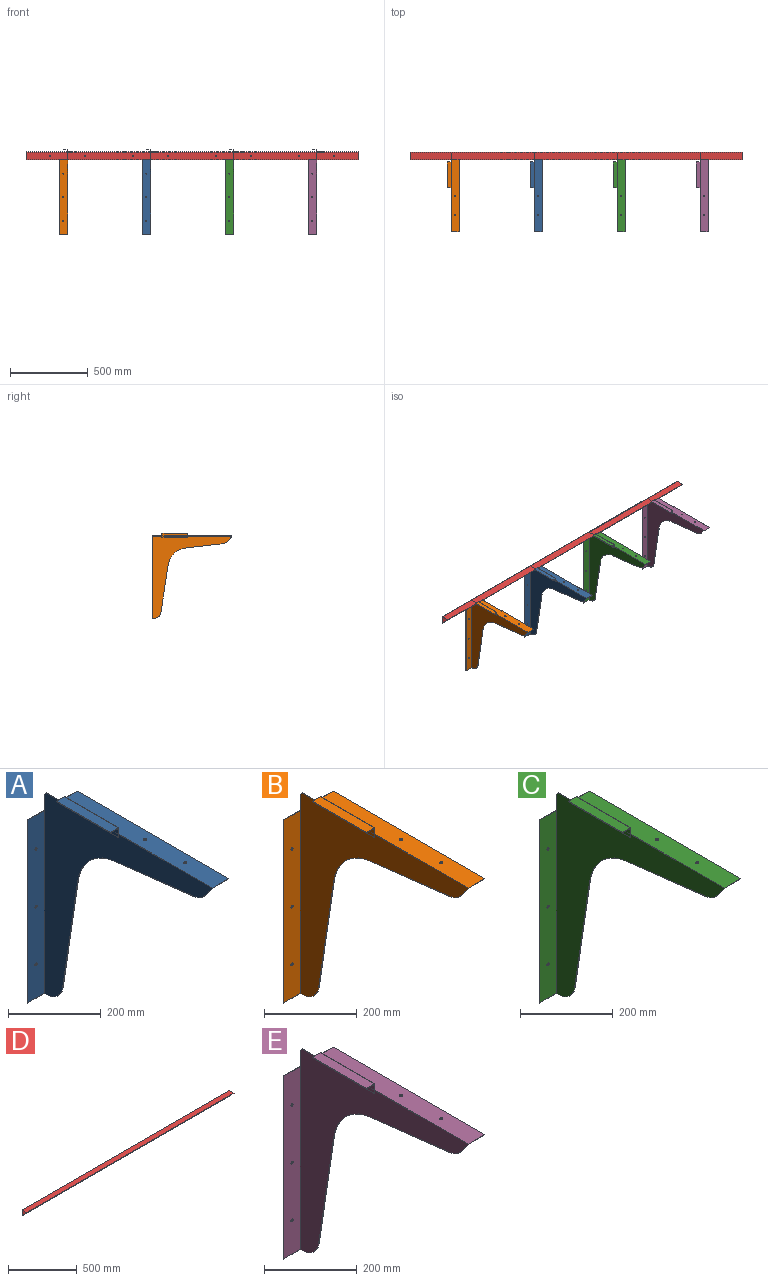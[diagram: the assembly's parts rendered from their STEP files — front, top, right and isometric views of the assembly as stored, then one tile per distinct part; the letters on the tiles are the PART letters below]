
ASSEMBLY  parts=5 mates=4
PART A: 33 faces, bbox 101.6x513.2x550.9 mm
  f0: plane 165.1x23.81mm, normal (-1,0,0), area 3931.4mm2, adj f2,f3,f4,f6
  f1: plane 165.1x25.4mm, normal (0,0,1), area 4193.5mm2, adj f2,f4,f5,f7
  f2: plane 25.4x25.4mm, normal (0,1,0), area 78.1mm2, adj f0,f1,f3,f5,f6,f7,f19
  f3: plane 165.1x1.59mm, normal (0,0,-1), area 262.1mm2, adj f0,f2,f4,f19
  f4: plane 25.4x25.4mm, normal (0,-1,0), area 78.1mm2, adj f0,f1,f3,f5,f6,f7,f19
  f5: plane 165.1x17.46mm, normal (1,0,0), area 2883.1mm2, adj f1,f2,f4,f22
  f6: plane 165.1x23.81mm, normal (0,0,-1), area 3931.4mm2, adj f0,f2,f4,f7
  f7: plane 165.1x1.59mm, normal (-1,0,0), area 262.1mm2, adj f1,f2,f4,f6
  f8: plane 42.86x1.59mm, normal (0,0,1), area 68mm2, adj f9,f18,f19,f21
  f9: plane 6.35x6.35mm, normal (0,0.71,0.71), area 14.3mm2, adj f8,f17,f18,f19
  f10: plane 50.8x30mm, normal (0,-0.81,-0.59), area 155.8mm2, adj f11,f18,f19,f20,f22,f23
  f11: cylinder r=50.8mm len=35.21mm, axis (-1,0,0), area 66.5mm2, adj f10,f12,f18,f19
  f12: plane 241.42x27.7mm, normal (0,-0.11,-0.99), area 385.8mm2, adj f11,f13,f18,f19
  f13: cylinder r=127mm len=111.09mm, axis (-1,0,0), area 263.3mm2, adj f12,f14,f18,f19
  f14: plane 304.89x46.19mm, normal (0,-0.99,-0.15), area 489.5mm2, adj f13,f15,f18,f19
  f15: cylinder r=50.8mm len=50.23mm, axis (-1,0,0), area 114.6mm2, adj f14,f16,f18,f19
  f16: plane 52.39x7.12mm, normal (0,0,-1), area 91.9mm2, adj f15,f18,f19,f24,f25,f27
  f17: plane 42.86x1.59mm, normal (0,1,0), area 68mm2, adj f9,f18,f19,f26
  f18: plane 531.81x512.03mm, normal (1,0,0), area 74022.7mm2, adj f8,f9,f10,f11,f12,f13,f14,f15
  f19: plane 533.4x511.61mm, normal (-1,0,0), area 72679.2mm2, adj f2,f3,f4,f8,f9,f10,f11,f12
  f20: plane 461.23x49.21mm, normal (0,0,-1), area 22626.8mm2, adj f10,f18,f21,f23,f31,f32
  f21: plane 50.8x1.59mm, normal (0,1,0), area 80.6mm2, adj f8,f19,f20,f22,f23
  f22: plane 462.4x50.8mm, normal (0,0,1), area 23418mm2, adj f5,f10,f19,f21,f23,f31,f32
  f23: plane 462.4x1.59mm, normal (1,0,0), area 733.1mm2, adj f10,f20,f21,f22
  f24: plane 482.6x50.8mm, normal (0,-1,0), area 24421.1mm2, adj f16,f19,f26,f27,f28,f29,f30
  f25: plane 482.6x52.39mm, normal (0,1,0), area 25187.2mm2, adj f16,f18,f26,f27,f28,f29,f30
  f26: plane 52.39x1.59mm, normal (0,0,1), area 83.2mm2, adj f17,f18,f24,f25,f27
  f27: plane 482.6x1.59mm, normal (-1,0,0), area 766.1mm2, adj f16,f24,f25,f26
  f28: cylinder r=3.17mm len=6.35mm, axis (0,-1,0), area 31.7mm2, adj f24,f25
  f29: cylinder r=3.17mm len=6.35mm, axis (0,-1,0), area 31.7mm2, adj f24,f25
  f30: cylinder r=3.17mm len=6.35mm, axis (0,-1,0), area 31.7mm2, adj f24,f25
  f31: cylinder r=3.38mm len=6.76mm, axis (0,0,-1), area 33.7mm2, adj f20,f22
  f32: cylinder r=3.38mm len=6.76mm, axis (0,0,-1), area 33.7mm2, adj f20,f22
PART B: 33 faces, bbox 101.6x513.2x550.9 mm
  f0: plane 165.1x23.81mm, normal (-1,0,0), area 3931.4mm2, adj f2,f3,f4,f6
  f1: plane 165.1x25.4mm, normal (0,0,1), area 4193.5mm2, adj f2,f4,f5,f7
  f2: plane 25.4x25.4mm, normal (0,1,0), area 78.1mm2, adj f0,f1,f3,f5,f6,f7,f19
  f3: plane 165.1x1.59mm, normal (0,0,-1), area 262.1mm2, adj f0,f2,f4,f19
  f4: plane 25.4x25.4mm, normal (0,-1,0), area 78.1mm2, adj f0,f1,f3,f5,f6,f7,f19
  f5: plane 165.1x17.46mm, normal (1,0,0), area 2883.1mm2, adj f1,f2,f4,f22
  f6: plane 165.1x23.81mm, normal (0,0,-1), area 3931.4mm2, adj f0,f2,f4,f7
  f7: plane 165.1x1.59mm, normal (-1,0,0), area 262.1mm2, adj f1,f2,f4,f6
  f8: plane 42.86x1.59mm, normal (0,0,1), area 68mm2, adj f9,f18,f19,f21
  f9: plane 6.35x6.35mm, normal (0,0.71,0.71), area 14.3mm2, adj f8,f17,f18,f19
  f10: plane 50.8x30mm, normal (0,-0.81,-0.59), area 155.8mm2, adj f11,f18,f19,f20,f22,f23
  f11: cylinder r=50.8mm len=35.21mm, axis (-1,0,0), area 66.5mm2, adj f10,f12,f18,f19
  f12: plane 241.42x27.7mm, normal (0,-0.11,-0.99), area 385.8mm2, adj f11,f13,f18,f19
  f13: cylinder r=127mm len=111.09mm, axis (-1,0,0), area 263.3mm2, adj f12,f14,f18,f19
  f14: plane 304.89x46.19mm, normal (0,-0.99,-0.15), area 489.5mm2, adj f13,f15,f18,f19
  f15: cylinder r=50.8mm len=50.23mm, axis (-1,0,0), area 114.6mm2, adj f14,f16,f18,f19
  f16: plane 52.39x7.12mm, normal (0,0,-1), area 91.9mm2, adj f15,f18,f19,f24,f25,f27
  f17: plane 42.86x1.59mm, normal (0,1,0), area 68mm2, adj f9,f18,f19,f26
  f18: plane 531.81x512.03mm, normal (1,0,0), area 74022.7mm2, adj f8,f9,f10,f11,f12,f13,f14,f15
  f19: plane 533.4x511.61mm, normal (-1,0,0), area 72679.2mm2, adj f2,f3,f4,f8,f9,f10,f11,f12
  f20: plane 461.23x49.21mm, normal (0,0,-1), area 22626.8mm2, adj f10,f18,f21,f23,f31,f32
  f21: plane 50.8x1.59mm, normal (0,1,0), area 80.6mm2, adj f8,f19,f20,f22,f23
  f22: plane 462.4x50.8mm, normal (0,0,1), area 23418mm2, adj f5,f10,f19,f21,f23,f31,f32
  f23: plane 462.4x1.59mm, normal (1,0,0), area 733.1mm2, adj f10,f20,f21,f22
  f24: plane 482.6x50.8mm, normal (0,-1,0), area 24421.1mm2, adj f16,f19,f26,f27,f28,f29,f30
  f25: plane 482.6x52.39mm, normal (0,1,0), area 25187.2mm2, adj f16,f18,f26,f27,f28,f29,f30
  f26: plane 52.39x1.59mm, normal (0,0,1), area 83.2mm2, adj f17,f18,f24,f25,f27
  f27: plane 482.6x1.59mm, normal (-1,0,0), area 766.1mm2, adj f16,f24,f25,f26
  f28: cylinder r=3.17mm len=6.35mm, axis (0,-1,0), area 31.7mm2, adj f24,f25
  f29: cylinder r=3.17mm len=6.35mm, axis (0,-1,0), area 31.7mm2, adj f24,f25
  f30: cylinder r=3.17mm len=6.35mm, axis (0,-1,0), area 31.7mm2, adj f24,f25
  f31: cylinder r=3.38mm len=6.76mm, axis (0,0,-1), area 33.7mm2, adj f20,f22
  f32: cylinder r=3.38mm len=6.76mm, axis (0,0,-1), area 33.7mm2, adj f20,f22
PART C: 33 faces, bbox 101.6x513.2x550.9 mm
  f0: plane 165.1x23.81mm, normal (-1,0,0), area 3931.4mm2, adj f2,f3,f4,f6
  f1: plane 165.1x25.4mm, normal (0,0,1), area 4193.5mm2, adj f2,f4,f5,f7
  f2: plane 25.4x25.4mm, normal (0,1,0), area 78.1mm2, adj f0,f1,f3,f5,f6,f7,f19
  f3: plane 165.1x1.59mm, normal (0,0,-1), area 262.1mm2, adj f0,f2,f4,f19
  f4: plane 25.4x25.4mm, normal (0,-1,0), area 78.1mm2, adj f0,f1,f3,f5,f6,f7,f19
  f5: plane 165.1x17.46mm, normal (1,0,0), area 2883.1mm2, adj f1,f2,f4,f22
  f6: plane 165.1x23.81mm, normal (0,0,-1), area 3931.4mm2, adj f0,f2,f4,f7
  f7: plane 165.1x1.59mm, normal (-1,0,0), area 262.1mm2, adj f1,f2,f4,f6
  f8: plane 42.86x1.59mm, normal (0,0,1), area 68mm2, adj f9,f18,f19,f21
  f9: plane 6.35x6.35mm, normal (0,0.71,0.71), area 14.3mm2, adj f8,f17,f18,f19
  f10: plane 50.8x30mm, normal (0,-0.81,-0.59), area 155.8mm2, adj f11,f18,f19,f20,f22,f23
  f11: cylinder r=50.8mm len=35.21mm, axis (-1,0,0), area 66.5mm2, adj f10,f12,f18,f19
  f12: plane 241.42x27.7mm, normal (0,-0.11,-0.99), area 385.8mm2, adj f11,f13,f18,f19
  f13: cylinder r=127mm len=111.09mm, axis (-1,0,0), area 263.3mm2, adj f12,f14,f18,f19
  f14: plane 304.89x46.19mm, normal (0,-0.99,-0.15), area 489.5mm2, adj f13,f15,f18,f19
  f15: cylinder r=50.8mm len=50.23mm, axis (-1,0,0), area 114.6mm2, adj f14,f16,f18,f19
  f16: plane 52.39x7.12mm, normal (0,0,-1), area 91.9mm2, adj f15,f18,f19,f24,f25,f27
  f17: plane 42.86x1.59mm, normal (0,1,0), area 68mm2, adj f9,f18,f19,f26
  f18: plane 531.81x512.03mm, normal (1,0,0), area 74022.7mm2, adj f8,f9,f10,f11,f12,f13,f14,f15
  f19: plane 533.4x511.61mm, normal (-1,0,0), area 72679.2mm2, adj f2,f3,f4,f8,f9,f10,f11,f12
  f20: plane 461.23x49.21mm, normal (0,0,-1), area 22626.8mm2, adj f10,f18,f21,f23,f31,f32
  f21: plane 50.8x1.59mm, normal (0,1,0), area 80.6mm2, adj f8,f19,f20,f22,f23
  f22: plane 462.4x50.8mm, normal (0,0,1), area 23418mm2, adj f5,f10,f19,f21,f23,f31,f32
  f23: plane 462.4x1.59mm, normal (1,0,0), area 733.1mm2, adj f10,f20,f21,f22
  f24: plane 482.6x50.8mm, normal (0,-1,0), area 24421.1mm2, adj f16,f19,f26,f27,f28,f29,f30
  f25: plane 482.6x52.39mm, normal (0,1,0), area 25187.2mm2, adj f16,f18,f26,f27,f28,f29,f30
  f26: plane 52.39x1.59mm, normal (0,0,1), area 83.2mm2, adj f17,f18,f24,f25,f27
  f27: plane 482.6x1.59mm, normal (-1,0,0), area 766.1mm2, adj f16,f24,f25,f26
  f28: cylinder r=3.17mm len=6.35mm, axis (0,-1,0), area 31.7mm2, adj f24,f25
  f29: cylinder r=3.17mm len=6.35mm, axis (0,-1,0), area 31.7mm2, adj f24,f25
  f30: cylinder r=3.17mm len=6.35mm, axis (0,-1,0), area 31.7mm2, adj f24,f25
  f31: cylinder r=3.38mm len=6.76mm, axis (0,0,-1), area 33.7mm2, adj f20,f22
  f32: cylinder r=3.38mm len=6.76mm, axis (0,0,-1), area 33.7mm2, adj f20,f22
PART D: 16 faces, bbox 2133.6x50.8x50.8 mm
  f0: plane 2133.6x50.8mm, normal (0,0,1), area 108386.9mm2, adj f1,f5,f6,f7
  f1: plane 2133.6x1.59mm, normal (0,-1,0), area 3387.1mm2, adj f0,f2,f6,f7
  f2: plane 2133.6x49.21mm, normal (0,0,-1), area 104999.8mm2, adj f1,f3,f6,f7
  f3: plane 2133.6x49.21mm, normal (0,-1,0), area 104746.4mm2, adj f2,f4,f6,f7,f8,f9,f10,f11
  f4: plane 2133.6x1.59mm, normal (0,0,-1), area 3387.1mm2, adj f3,f5,f6,f7
  f5: plane 2133.6x50.8mm, normal (0,1,0), area 108133.5mm2, adj f0,f4,f6,f7,f8,f9,f10,f11
  f6: plane 50.8x50.8mm, normal (-1,0,0), area 158.8mm2, adj f0,f1,f2,f3,f4,f5
  f7: plane 50.8x50.8mm, normal (1,0,0), area 158.8mm2, adj f0,f1,f2,f3,f4,f5
  f8: cylinder r=3.17mm len=6.35mm, axis (0,-1,0), area 31.7mm2, adj f3,f5
  f9: cylinder r=3.17mm len=6.35mm, axis (0,-1,0), area 31.7mm2, adj f3,f5
  f10: cylinder r=3.17mm len=6.35mm, axis (0,-1,0), area 31.7mm2, adj f3,f5
  f11: cylinder r=3.17mm len=6.35mm, axis (0,-1,0), area 31.7mm2, adj f3,f5
  f12: cylinder r=3.17mm len=6.35mm, axis (0,-1,0), area 31.7mm2, adj f3,f5
  f13: cylinder r=3.17mm len=6.35mm, axis (0,-1,0), area 31.7mm2, adj f3,f5
  f14: cylinder r=3.17mm len=6.35mm, axis (0,-1,0), area 31.7mm2, adj f3,f5
  f15: cylinder r=3.17mm len=6.35mm, axis (0,-1,0), area 31.7mm2, adj f3,f5
PART E: 33 faces, bbox 101.6x513.2x550.9 mm
  f0: plane 165.1x23.81mm, normal (-1,0,0), area 3931.4mm2, adj f2,f3,f4,f6
  f1: plane 165.1x25.4mm, normal (0,0,1), area 4193.5mm2, adj f2,f4,f5,f7
  f2: plane 25.4x25.4mm, normal (0,1,0), area 78.1mm2, adj f0,f1,f3,f5,f6,f7,f19
  f3: plane 165.1x1.59mm, normal (0,0,-1), area 262.1mm2, adj f0,f2,f4,f19
  f4: plane 25.4x25.4mm, normal (0,-1,0), area 78.1mm2, adj f0,f1,f3,f5,f6,f7,f19
  f5: plane 165.1x17.46mm, normal (1,0,0), area 2883.1mm2, adj f1,f2,f4,f22
  f6: plane 165.1x23.81mm, normal (0,0,-1), area 3931.4mm2, adj f0,f2,f4,f7
  f7: plane 165.1x1.59mm, normal (-1,0,0), area 262.1mm2, adj f1,f2,f4,f6
  f8: plane 42.86x1.59mm, normal (0,0,1), area 68mm2, adj f9,f18,f19,f21
  f9: plane 6.35x6.35mm, normal (0,0.71,0.71), area 14.3mm2, adj f8,f17,f18,f19
  f10: plane 50.8x30mm, normal (0,-0.81,-0.59), area 155.8mm2, adj f11,f18,f19,f20,f22,f23
  f11: cylinder r=50.8mm len=35.21mm, axis (-1,0,0), area 66.5mm2, adj f10,f12,f18,f19
  f12: plane 241.42x27.7mm, normal (0,-0.11,-0.99), area 385.8mm2, adj f11,f13,f18,f19
  f13: cylinder r=127mm len=111.09mm, axis (-1,0,0), area 263.3mm2, adj f12,f14,f18,f19
  f14: plane 304.89x46.19mm, normal (0,-0.99,-0.15), area 489.5mm2, adj f13,f15,f18,f19
  f15: cylinder r=50.8mm len=50.23mm, axis (-1,0,0), area 114.6mm2, adj f14,f16,f18,f19
  f16: plane 52.39x7.12mm, normal (0,0,-1), area 91.9mm2, adj f15,f18,f19,f24,f25,f27
  f17: plane 42.86x1.59mm, normal (0,1,0), area 68mm2, adj f9,f18,f19,f26
  f18: plane 531.81x512.03mm, normal (1,0,0), area 74022.7mm2, adj f8,f9,f10,f11,f12,f13,f14,f15
  f19: plane 533.4x511.61mm, normal (-1,0,0), area 72679.2mm2, adj f2,f3,f4,f8,f9,f10,f11,f12
  f20: plane 461.23x49.21mm, normal (0,0,-1), area 22626.8mm2, adj f10,f18,f21,f23,f31,f32
  f21: plane 50.8x1.59mm, normal (0,1,0), area 80.6mm2, adj f8,f19,f20,f22,f23
  f22: plane 462.4x50.8mm, normal (0,0,1), area 23418mm2, adj f5,f10,f19,f21,f23,f31,f32
  f23: plane 462.4x1.59mm, normal (1,0,0), area 733.1mm2, adj f10,f20,f21,f22
  f24: plane 482.6x50.8mm, normal (0,-1,0), area 24421.1mm2, adj f16,f19,f26,f27,f28,f29,f30
  f25: plane 482.6x52.39mm, normal (0,1,0), area 25187.2mm2, adj f16,f18,f26,f27,f28,f29,f30
  f26: plane 52.39x1.59mm, normal (0,0,1), area 83.2mm2, adj f17,f18,f24,f25,f27
  f27: plane 482.6x1.59mm, normal (-1,0,0), area 766.1mm2, adj f16,f24,f25,f26
  f28: cylinder r=3.17mm len=6.35mm, axis (0,-1,0), area 31.7mm2, adj f24,f25
  f29: cylinder r=3.17mm len=6.35mm, axis (0,-1,0), area 31.7mm2, adj f24,f25
  f30: cylinder r=3.17mm len=6.35mm, axis (0,-1,0), area 31.7mm2, adj f24,f25
  f31: cylinder r=3.38mm len=6.76mm, axis (0,0,-1), area 33.7mm2, adj f20,f22
  f32: cylinder r=3.38mm len=6.76mm, axis (0,0,-1), area 33.7mm2, adj f20,f22
PLACE A t=(96.67,-113.64,181.38)mm
PLACE B t=(96.67,-113.64,181.38)mm
PLACE C t=(96.67,-113.64,181.38)mm
PLACE D t=(122.87,-113.64,181.38)mm fixed
PLACE E t=(96.67,-113.64,181.38)mm
MATE fastened A.f17 <-> D.f3  axis (0,1,0) through (-138.33,32.35,173.44)mm
MATE fastened C.f22 <-> A.f22  axis (0,0,1) through (393.49,-479.26,181.38)mm
MATE fastened E.f22 <-> C.f22  axis (0,0,1) through (926.89,-479.26,181.38)mm
MATE fastened A.f22 <-> B.f22  axis (0,0,1) through (-139.91,-479.26,181.38)mm
